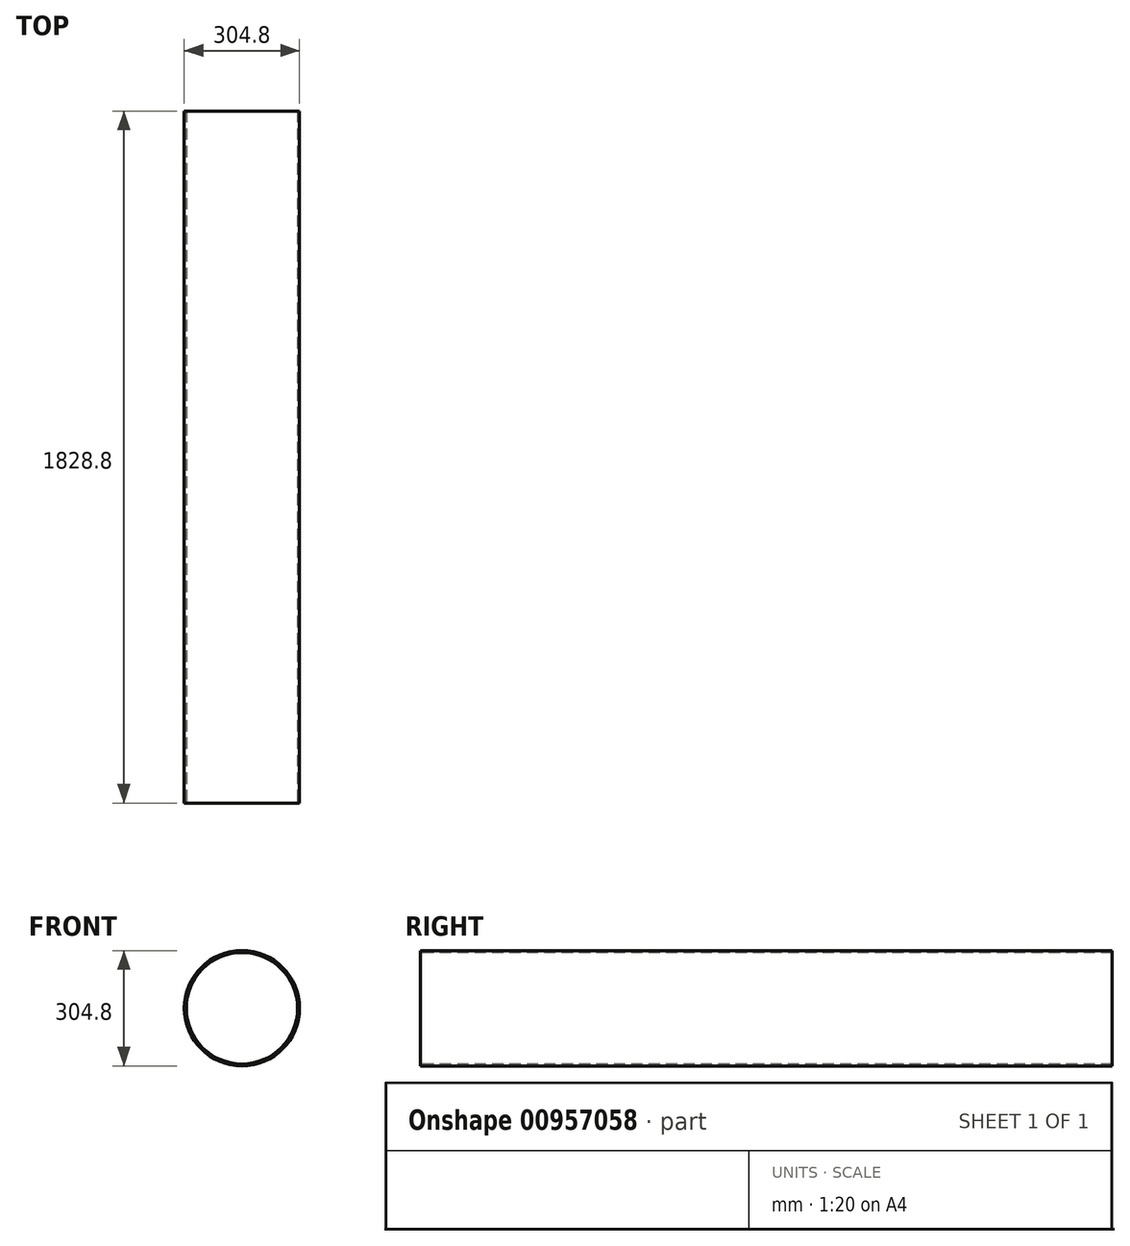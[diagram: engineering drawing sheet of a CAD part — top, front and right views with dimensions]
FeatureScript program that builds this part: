
annotation { "Feature Type Name" : "Feature", "Feature Type Description" : "" }
export const myFeature = defineFeature(function(context is Context, id is Id, definition is map)
    precondition{}
    {
        {
            var Q0;
            Q0=qCreatedBy(makeId("Front.planeOp"),FACE);
            var sketch = newSketch(context, id + "F0", { "sketchPlane" : qUnion([Q0])});
            skCircle(sketch, "E0", {"center": v(0, 0) * mm, "radius": 152.4 * mm});
            skCircle(sketch, "E1", {"center": v(0, 0) * mm, "radius": 147.27 * mm});
            skSolve(sketch);
        }
        {
            var Q0;
            Q0=sQuery(id+"F0.wireOp",EDGE,"E0");
            var Q1;
            Q1=sQuery(id+"F0.wireOp",EDGE,"E1");
            extrude(context, id + "F1", {"bodyType" : ToolBodyType.SURFACE, "surfaceEntities" : qUnion([Q0, Q1]), "depth" : 1828.8 * mm, "offsetDistance" : 25.4 * mm});
        }
    });
